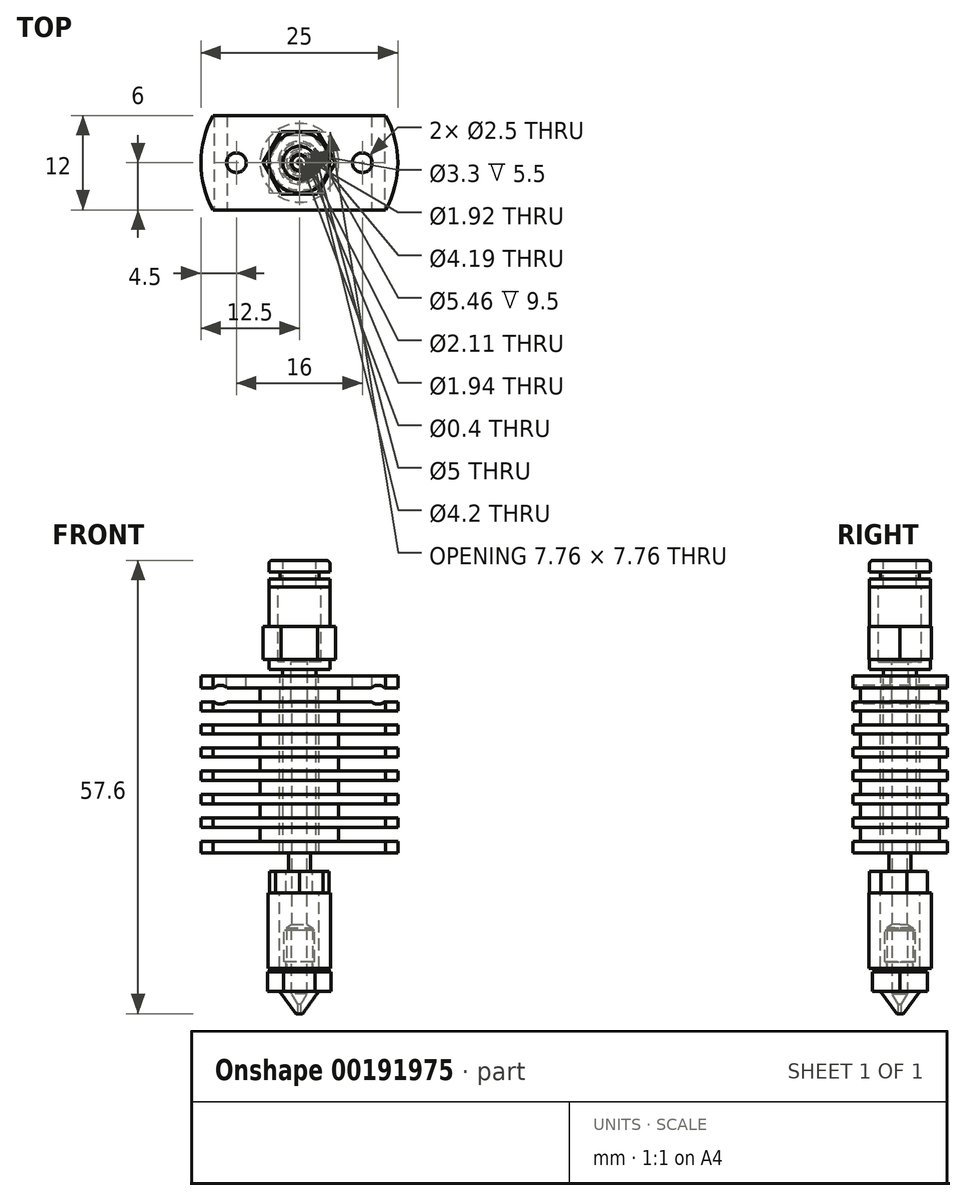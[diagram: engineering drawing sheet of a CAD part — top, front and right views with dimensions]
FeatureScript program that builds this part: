
annotation { "Feature Type Name" : "Feature", "Feature Type Description" : "" }
export const myFeature = defineFeature(function(context is Context, id is Id, definition is map)
    precondition{}
    {
        {
            var Q0;
            Q0=qCreatedBy(makeId("Front.planeOp"),FACE);
            var sketch = newSketch(context, id + "F0", { "sketchPlane" : qUnion([Q0])});
            skLineSegment(sketch, "E0.bottom", {"start": v(0, 0) * mm, "end": v(5, 0) * mm});
            skLineSegment(sketch, "E0.top", {"start": v(0, -22.5) * mm, "end": v(5, -22.5) * mm});
            skLineSegment(sketch, "E0.left", {"start": v(0, 0) * mm, "end": v(0, -22.5) * mm});
            skLineSegment(sketch, "E0.right", {"start": v(5, 0) * mm, "end": v(5, -22.5) * mm});
            skLineSegment(sketch, "E1", {"start": v(0, 43.67) * mm, "end": v(0, -73.74) * mm, "construction": true});
            skLineSegment(sketch, "E2.bottom", {"start": v(0, 0) * mm, "end": v(12.5, 0) * mm});
            skLineSegment(sketch, "E2.top", {"start": v(0, -1.5) * mm, "end": v(12.5, -1.5) * mm});
            skLineSegment(sketch, "E2.left", {"start": v(0, 0) * mm, "end": v(0, -1.5) * mm});
            skLineSegment(sketch, "E2.right", {"start": v(12.5, 0) * mm, "end": v(12.5, -1.5) * mm});
            skLineSegment(sketch, "E3.bottom", {"start": v(0, -3.27) * mm, "end": v(12.5, -3.27) * mm});
            skLineSegment(sketch, "E3.top", {"start": v(0, -4.42) * mm, "end": v(12.5, -4.42) * mm});
            skLineSegment(sketch, "E3.left", {"start": v(0, -3.27) * mm, "end": v(0, -4.42) * mm});
            skLineSegment(sketch, "E3.right", {"start": v(12.5, -3.27) * mm, "end": v(12.5, -4.42) * mm});
            skLineSegment(sketch, "E4.bottom", {"start": v(0, -6.2) * mm, "end": v(12.5, -6.2) * mm});
            skLineSegment(sketch, "E4.top", {"start": v(0, -7.34) * mm, "end": v(12.5, -7.34) * mm});
            skLineSegment(sketch, "E4.left", {"start": v(0, -6.2) * mm, "end": v(0, -7.34) * mm});
            skLineSegment(sketch, "E4.right", {"start": v(12.5, -6.2) * mm, "end": v(12.5, -7.34) * mm});
            skLineSegment(sketch, "E5.bottom", {"start": v(0, -9.11) * mm, "end": v(12.5, -9.11) * mm});
            skLineSegment(sketch, "E5.top", {"start": v(0, -10.31) * mm, "end": v(12.5, -10.31) * mm});
            skLineSegment(sketch, "E5.left", {"start": v(0, -9.11) * mm, "end": v(0, -10.31) * mm});
            skLineSegment(sketch, "E5.right", {"start": v(12.5, -9.11) * mm, "end": v(12.5, -10.31) * mm});
            skLineSegment(sketch, "E6.bottom", {"start": v(0, -12.09) * mm, "end": v(12.5, -12.09) * mm});
            skLineSegment(sketch, "E6.top", {"start": v(0, -13.29) * mm, "end": v(12.5, -13.29) * mm});
            skLineSegment(sketch, "E6.left", {"start": v(0, -12.09) * mm, "end": v(0, -13.29) * mm});
            skLineSegment(sketch, "E6.right", {"start": v(12.5, -12.09) * mm, "end": v(12.5, -13.29) * mm});
            skLineSegment(sketch, "E7.bottom", {"start": v(0, -15.06) * mm, "end": v(12.5, -15.06) * mm});
            skLineSegment(sketch, "E7.top", {"start": v(0, -16.26) * mm, "end": v(12.5, -16.26) * mm});
            skLineSegment(sketch, "E7.left", {"start": v(0, -15.06) * mm, "end": v(0, -16.26) * mm});
            skLineSegment(sketch, "E7.right", {"start": v(12.5, -15.06) * mm, "end": v(12.5, -16.26) * mm});
            skLineSegment(sketch, "E8.bottom", {"start": v(0, -18.03) * mm, "end": v(12.5, -18.03) * mm});
            skLineSegment(sketch, "E8.top", {"start": v(0, -19.23) * mm, "end": v(12.5, -19.23) * mm});
            skLineSegment(sketch, "E8.left", {"start": v(0, -18.03) * mm, "end": v(0, -19.23) * mm});
            skLineSegment(sketch, "E8.right", {"start": v(12.5, -18.03) * mm, "end": v(12.5, -19.23) * mm});
            skLineSegment(sketch, "E9.bottom", {"start": v(0, -21) * mm, "end": v(12.5, -21) * mm});
            skLineSegment(sketch, "E9.top", {"start": v(0, -22.5) * mm, "end": v(12.5, -22.5) * mm});
            skLineSegment(sketch, "E9.left", {"start": v(0, -21) * mm, "end": v(0, -22.5) * mm});
            skLineSegment(sketch, "E9.right", {"start": v(12.5, -21) * mm, "end": v(12.5, -22.5) * mm});
            skLineSegment(sketch, "E10", {"start": v(12.5, -21) * mm, "end": v(12.5, -19.23) * mm, "construction": true});
            skLineSegment(sketch, "E11", {"start": v(12.5, -18.03) * mm, "end": v(12.5, -16.26) * mm, "construction": true});
            skLineSegment(sketch, "E12", {"start": v(12.5, -15.06) * mm, "end": v(12.5, -13.29) * mm, "construction": true});
            skLineSegment(sketch, "E13", {"start": v(12.5, -12.09) * mm, "end": v(12.5, -10.31) * mm, "construction": true});
            skLineSegment(sketch, "E14", {"start": v(12.5, -9.11) * mm, "end": v(12.5, -7.34) * mm, "construction": true});
            skLineSegment(sketch, "E15", {"start": v(12.5, -6.2) * mm, "end": v(12.5, -4.42) * mm, "construction": true});
            skLineSegment(sketch, "E16", {"start": v(12.5, -3.27) * mm, "end": v(12.5, -1.5) * mm, "construction": true});
            skSolve(sketch);
        }
        {
            var Q0;
            Q0=qSketchRegion(id+"F0",true);
            var Q1;
            Q1=sQuery(id+"F0.wireOp",EDGE,"E1");
            revolve(context, id + "F1", {"entities" : qUnion([Q0]), "axis" : qUnion([Q1]), "revolveType" : RevolveType.FULL});
        }
        {
            var Q0;
            Q0=qCreatedBy(makeId("Top.planeOp"),FACE);
            var sketch = newSketch(context, id + "F2", { "sketchPlane" : qUnion([Q0])});
            skLineSegment(sketch, "E17.bottom", {"start": v(-10.97, -6) * mm, "end": v(10.97, -6) * mm});
            skLineSegment(sketch, "E17.top", {"start": v(-10.97, -12.5) * mm, "end": v(10.97, -12.5) * mm});
            skLineSegment(sketch, "E17.left", {"start": v(-10.97, -6) * mm, "end": v(-10.97, -12.5) * mm});
            skLineSegment(sketch, "E17.right", {"start": v(10.97, -6) * mm, "end": v(10.97, -12.5) * mm});
            skLineSegment(sketch, "E18.bottom", {"start": v(-10.97, 6) * mm, "end": v(10.97, 6) * mm});
            skLineSegment(sketch, "E18.top", {"start": v(-10.97, 12.5) * mm, "end": v(10.97, 12.5) * mm});
            skLineSegment(sketch, "E18.left", {"start": v(-10.97, 6) * mm, "end": v(-10.97, 12.5) * mm});
            skLineSegment(sketch, "E18.right", {"start": v(10.97, 6) * mm, "end": v(10.97, 12.5) * mm});
            skSolve(sketch);
        }
        {
            var Q0;
            Q0=qSketchRegion(id+"F2",true);
            extrude(context, id + "F3", {"entities" : qUnion([Q0]), "operationType" : NewBodyOperationType.REMOVE, "endBound" : BoundingType.THROUGH_ALL, "oppositeDirection" : true, "depth" : 25 * mm});
        }
        {
            var Q0;
            Q0=makeQuery(id+"F1.opRevolve","SWEPT_FACE",FACE,{"disambiguationData":[OSD([sQuery(id+"F0.wireOp",EDGE,"E2.bottom")])]});
            var sketch = newSketch(context, id + "F4", { "sketchPlane" : qUnion([Q0])});
            skPoint(sketch, "E19", {"position": v(0, 0) * mm});
            skPoint(sketch, "E20", {"position": v(-8, 0) * mm});
            skPoint(sketch, "E21", {"position": v(8, 0) * mm});
            skSolve(sketch);
        }
        {
            var Q0;
            Q0=sQuery(id+"F4.wireOp",VERTEX,"E19");
            var Q1;
            Q1=makeQuery(id+"F1.opRevolve","SWEPT_BODY",BODY,{"disambiguationData":[OSD([sQuery(id+"F0.wireOp",EDGE,"E0.left"),sQuery(id+"F0.wireOp",EDGE,"E0.right"),sQuery(id+"F0.wireOp",EDGE,"E2.bottom"),sQuery(id+"F0.wireOp",EDGE,"E2.top"),sQuery(id+"F0.wireOp",EDGE,"E2.left"),sQuery(id+"F0.wireOp",EDGE,"E2.right"),sQuery(id+"F0.wireOp",EDGE,"E3.bottom"),sQuery(id+"F0.wireOp",EDGE,"E3.top"),sQuery(id+"F0.wireOp",EDGE,"E3.left"),sQuery(id+"F0.wireOp",EDGE,"E3.right"),sQuery(id+"F0.wireOp",EDGE,"E4.bottom"),sQuery(id+"F0.wireOp",EDGE,"E4.top"),sQuery(id+"F0.wireOp",EDGE,"E4.left"),sQuery(id+"F0.wireOp",EDGE,"E4.right"),sQuery(id+"F0.wireOp",EDGE,"E5.bottom"),sQuery(id+"F0.wireOp",EDGE,"E5.top"),sQuery(id+"F0.wireOp",EDGE,"E5.left"),sQuery(id+"F0.wireOp",EDGE,"E5.right"),sQuery(id+"F0.wireOp",EDGE,"E6.bottom"),sQuery(id+"F0.wireOp",EDGE,"E6.top"),sQuery(id+"F0.wireOp",EDGE,"E6.left"),sQuery(id+"F0.wireOp",EDGE,"E6.right"),sQuery(id+"F0.wireOp",EDGE,"E7.bottom"),sQuery(id+"F0.wireOp",EDGE,"E7.top"),sQuery(id+"F0.wireOp",EDGE,"E7.left"),sQuery(id+"F0.wireOp",EDGE,"E7.right"),sQuery(id+"F0.wireOp",EDGE,"E8.bottom"),sQuery(id+"F0.wireOp",EDGE,"E8.top"),sQuery(id+"F0.wireOp",EDGE,"E8.left"),sQuery(id+"F0.wireOp",EDGE,"E8.right"),sQuery(id+"F0.wireOp",EDGE,"E9.bottom"),sQuery(id+"F0.wireOp",EDGE,"E9.top"),sQuery(id+"F0.wireOp",EDGE,"E9.left"),sQuery(id+"F0.wireOp",EDGE,"E9.right")])]});
            hole(context, id + "F5", {"style" : HoleStyle.SIMPLE, "endStyle" : HoleEndStyle.THROUGH, "standardTappedOrClearance" : lookupTablePath({ "standard" : "ISO", "engagement" : "75%", "pitch" : "0.8 mm", "size" : "M5", "type" : "Tapped" }), "standardBlindInLast" : lookupTablePath({ "standard" : "ISO", "engagement" : "75%", "pitch" : "0.8 mm", "size" : "M5", "type" : "Tapped" }), "holeDiameter" : 4.2 * mm, "locations" : qUnion([Q0]), "scope" : qUnion([Q1]), "isTappedThrough" : true, "majorDiameter" : 5 * mm, "showTappedDepth" : true});
        }
        {
            var Q0;
            Q0=sQuery(id+"F4.wireOp",VERTEX,"E20");
            var Q1;
            Q1=sQuery(id+"F4.wireOp",VERTEX,"E21");
            var Q2;
            Q2=makeQuery(id+"F1.opRevolve","SWEPT_BODY",BODY,{"disambiguationData":[OSD([sQuery(id+"F0.wireOp",EDGE,"E0.left"),sQuery(id+"F0.wireOp",EDGE,"E0.right"),sQuery(id+"F0.wireOp",EDGE,"E2.bottom"),sQuery(id+"F0.wireOp",EDGE,"E2.top"),sQuery(id+"F0.wireOp",EDGE,"E2.left"),sQuery(id+"F0.wireOp",EDGE,"E2.right"),sQuery(id+"F0.wireOp",EDGE,"E3.bottom"),sQuery(id+"F0.wireOp",EDGE,"E3.top"),sQuery(id+"F0.wireOp",EDGE,"E3.left"),sQuery(id+"F0.wireOp",EDGE,"E3.right"),sQuery(id+"F0.wireOp",EDGE,"E4.bottom"),sQuery(id+"F0.wireOp",EDGE,"E4.top"),sQuery(id+"F0.wireOp",EDGE,"E4.left"),sQuery(id+"F0.wireOp",EDGE,"E4.right"),sQuery(id+"F0.wireOp",EDGE,"E5.bottom"),sQuery(id+"F0.wireOp",EDGE,"E5.top"),sQuery(id+"F0.wireOp",EDGE,"E5.left"),sQuery(id+"F0.wireOp",EDGE,"E5.right"),sQuery(id+"F0.wireOp",EDGE,"E6.bottom"),sQuery(id+"F0.wireOp",EDGE,"E6.top"),sQuery(id+"F0.wireOp",EDGE,"E6.left"),sQuery(id+"F0.wireOp",EDGE,"E6.right"),sQuery(id+"F0.wireOp",EDGE,"E7.bottom"),sQuery(id+"F0.wireOp",EDGE,"E7.top"),sQuery(id+"F0.wireOp",EDGE,"E7.left"),sQuery(id+"F0.wireOp",EDGE,"E7.right"),sQuery(id+"F0.wireOp",EDGE,"E8.bottom"),sQuery(id+"F0.wireOp",EDGE,"E8.top"),sQuery(id+"F0.wireOp",EDGE,"E8.left"),sQuery(id+"F0.wireOp",EDGE,"E8.right"),sQuery(id+"F0.wireOp",EDGE,"E9.bottom"),sQuery(id+"F0.wireOp",EDGE,"E9.top"),sQuery(id+"F0.wireOp",EDGE,"E9.left"),sQuery(id+"F0.wireOp",EDGE,"E9.right")])]});
            hole(context, id + "F6", {"style" : HoleStyle.SIMPLE, "endStyle" : HoleEndStyle.BLIND, "standardTappedOrClearance" : lookupTablePath({ "standard" : "ISO", "engagement" : "75%", "pitch" : "0.5 mm", "size" : "M3", "type" : "Tapped" }), "standardBlindInLast" : lookupTablePath({ "standard" : "ISO", "engagement" : "75%", "pitch" : "0.5 mm", "size" : "M3", "type" : "Tapped" }), "holeDiameter" : 2.5 * mm, "holeDepth" : 2 * mm, "startFromSketch" : true, "locations" : qUnion([Q0, Q1]), "scope" : qUnion([Q2]), "majorDiameter" : 3 * mm});
        }
        {
            var Q0;
            Q0=qCreatedBy(makeId("Front.planeOp"),FACE);
            var sketch = newSketch(context, id + "F7", { "sketchPlane" : qUnion([Q0])});
            skLineSegment(sketch, "E22.bottom", {"start": v(0, -3.22) * mm, "end": v(1.39, -3.22) * mm});
            skLineSegment(sketch, "E22.top", {"start": v(0, -37.5) * mm, "end": v(1.39, -37.5) * mm});
            skLineSegment(sketch, "E22.left", {"start": v(0, -3.22) * mm, "end": v(0, -37.5) * mm});
            skLineSegment(sketch, "E22.right", {"start": v(1.38, -3.22) * mm, "end": v(1.39, -37.5) * mm});
            skLineSegment(sketch, "E23", {"start": v(0, 12.08) * mm, "end": v(0, -40.12) * mm, "construction": true});
            skLineSegment(sketch, "E24.bottom", {"start": v(0, -37.5) * mm, "end": v(2.5, -37.5) * mm});
            skLineSegment(sketch, "E24.top", {"start": v(0, -24.8) * mm, "end": v(2.5, -24.8) * mm});
            skLineSegment(sketch, "E24.left", {"start": v(0, -37.5) * mm, "end": v(0, -24.8) * mm});
            skLineSegment(sketch, "E24.right", {"start": v(2.5, -37.5) * mm, "end": v(2.5, -24.8) * mm});
            skLineSegment(sketch, "E25.bottom", {"start": v(0, -3.22) * mm, "end": v(2.5, -3.22) * mm});
            skLineSegment(sketch, "E25.top", {"start": v(0, -22.5) * mm, "end": v(2.5, -22.5) * mm});
            skLineSegment(sketch, "E25.left", {"start": v(0, -3.22) * mm, "end": v(0, -22.5) * mm});
            skLineSegment(sketch, "E25.right", {"start": v(2.5, -3.22) * mm, "end": v(2.5, -22.5) * mm});
            skSolve(sketch);
        }
        {
            var Q0;
            Q0=qSketchRegion(id+"F7",true);
            var Q1;
            Q1=sQuery(id+"F7.wireOp",EDGE,"E23");
            revolve(context, id + "F8", {"entities" : qUnion([Q0]), "axis" : qUnion([Q1]), "revolveType" : RevolveType.FULL});
        }
        {
            var Q0;
            Q0=makeQuery(id+"F8.opRevolve","SWEPT_FACE",FACE,{"disambiguationData":[OSD([sQuery(id+"F7.wireOp",EDGE,"E24.top")])]});
            var sketch = newSketch(context, id + "F9", { "sketchPlane" : qUnion([Q0])});
            skCircle(sketch, "E26.cCircle", {"center": v(0, 0) * mm, "radius": 3.5 * mm, "construction": true});
            skLineSegment(sketch, "E26.0", {"start": v(1.69, 3.5) * mm, "end": v(3.79, 0.86) * mm});
            skLineSegment(sketch, "E26.1", {"start": v(3.79, 0.86) * mm, "end": v(3.04, -2.42) * mm});
            skLineSegment(sketch, "E26.2", {"start": v(3.04, -2.42) * mm, "end": v(0, -3.88) * mm});
            skLineSegment(sketch, "E26.3", {"start": v(0, -3.88) * mm, "end": v(-3.04, -2.42) * mm});
            skLineSegment(sketch, "E26.4", {"start": v(-3.04, -2.42) * mm, "end": v(-3.79, 0.86) * mm});
            skLineSegment(sketch, "E26.5", {"start": v(-3.79, 0.86) * mm, "end": v(-1.69, 3.5) * mm});
            skLineSegment(sketch, "E26.6", {"start": v(-1.69, 3.5) * mm, "end": v(1.69, 3.5) * mm});
            skPoint(sketch, "E26.0.midPoint", {"position": v(2.74, 2.18) * mm});
            skSolve(sketch);
        }
        {
            var Q0;
            Q0=qSketchRegion(id+"F9",true);
            extrude(context, id + "F10", {"entities" : qUnion([Q0]), "operationType" : NewBodyOperationType.ADD, "oppositeDirection" : true, "depth" : 2.75 * mm});
        }
        {
            var Q0;
            Q0=makeQuery(id+"F8.opRevolve","SWEPT_FACE",FACE,{"disambiguationData":[OSD([sQuery(id+"F7.wireOp",EDGE,"E24.bottom")])]});
            var sketch = newSketch(context, id + "F11", { "sketchPlane" : qUnion([Q0])});
            skPoint(sketch, "E27", {"position": v(0, 0) * mm});
            skSolve(sketch);
        }
        {
            var Q0;
            Q0=sQuery(id+"F11.wireOp",VERTEX,"E27");
            var Q1;
            Q1=makeQuery(id+"F8.opRevolve","SWEPT_BODY",BODY,{"disambiguationData":[OSD([sQuery(id+"F7.wireOp",EDGE,"E22.left"),sQuery(id+"F7.wireOp",EDGE,"E22.right"),sQuery(id+"F7.wireOp",EDGE,"E24.bottom"),sQuery(id+"F7.wireOp",EDGE,"E24.top"),sQuery(id+"F7.wireOp",EDGE,"E24.left"),sQuery(id+"F7.wireOp",EDGE,"E24.right"),sQuery(id+"F7.wireOp",EDGE,"E25.bottom"),sQuery(id+"F7.wireOp",EDGE,"E25.top"),sQuery(id+"F7.wireOp",EDGE,"E25.left"),sQuery(id+"F7.wireOp",EDGE,"E25.right")])]});
            hole(context, id + "F12", {"style" : HoleStyle.SIMPLE, "endStyle" : HoleEndStyle.BLIND, "standardTappedOrClearance" : lookupTablePath({ "standard" : "ISO", "engagement" : "75%", "pitch" : "0.7 mm", "size" : "M4", "type" : "Tapped" }), "standardBlindInLast" : lookupTablePath({ "standard" : "ISO", "engagement" : "75%", "pitch" : "0.7 mm", "size" : "M4", "type" : "Tapped" }), "holeDiameter" : 3.3 * mm, "holeDepth" : 5.5 * mm, "startFromSketch" : true, "locations" : qUnion([Q0]), "scope" : qUnion([Q1]), "majorDiameter" : 4 * mm});
        }
        {
            var Q0;
            Q0=makeQuery(id+"F8.opRevolve","SWEPT_FACE",FACE,{"disambiguationData":[OSD([sQuery(id+"F7.wireOp",EDGE,"E25.bottom")])]});
            var sketch = newSketch(context, id + "F13", { "sketchPlane" : qUnion([Q0])});
            skCircle(sketch, "E28", {"center": v(0, 0) * mm, "radius": 0.96 * mm});
            skSolve(sketch);
        }
        {
            var Q0;
            Q0=qSketchRegion(id+"F13",true);
            extrude(context, id + "F14", {"entities" : qUnion([Q0]), "operationType" : NewBodyOperationType.REMOVE, "endBound" : BoundingType.THROUGH_ALL, "oppositeDirection" : true, "depth" : 25 * mm});
        }
        {
            var Q0;
            Q0=makeQuery(id+"F10.opExtrude","CAP_FACE",FACE,{"disambiguationData":[OSD([sQuery(id+"F9.wireOp",EDGE,"E26.0"),sQuery(id+"F9.wireOp",EDGE,"E26.1"),sQuery(id+"F9.wireOp",EDGE,"E26.2"),sQuery(id+"F9.wireOp",EDGE,"E26.3"),sQuery(id+"F9.wireOp",EDGE,"E26.4"),sQuery(id+"F9.wireOp",EDGE,"E26.5"),sQuery(id+"F9.wireOp",EDGE,"E26.6")])],"isStart":false});
            var sketch = newSketch(context, id + "F15", { "sketchPlane" : qUnion([Q0])});
            skCircle(sketch, "E29", {"center": v(0, 0) * mm, "radius": 2.5 * mm});
            skCircle(sketch, "E30", {"center": v(0, 0) * mm, "radius": 3.96 * mm});
            skSolve(sketch);
        }
        {
            var Q0;
            Q0=qSketchRegion(id+"F15",true);
            extrude(context, id + "F16", {"entities" : qUnion([Q0]), "depth" : 9.6 * mm});
        }
        {
            var Q0;
            Q0=qCreatedBy(makeId("Front.planeOp"),FACE);
            var sketch = newSketch(context, id + "F17", { "sketchPlane" : qUnion([Q0])});
            skLineSegment(sketch, "E31", {"start": v(0, 4.14) * mm, "end": v(0, -44.2) * mm, "construction": true});
            skLineSegment(sketch, "E32.bottom", {"start": v(0.97, -32.3) * mm, "end": v(1.95, -32.3) * mm});
            skLineSegment(sketch, "E32.top", {"start": v(0.2, -42.9) * mm, "end": v(0.41, -42.9) * mm});
            skLineSegment(sketch, "E32.right", {"start": v(3.5, -37.57) * mm, "end": v(3.5, -40.04) * mm});
            skLineSegment(sketch, "E33", {"start": v(3.5, -37.57) * mm, "end": v(1.67, -37.57) * mm});
            skLineSegment(sketch, "E34", {"start": v(1.67, -37.57) * mm, "end": v(1.67, -36.3) * mm});
            skLineSegment(sketch, "E35", {"start": v(1.67, -36.3) * mm, "end": v(1.95, -36.3) * mm});
            skLineSegment(sketch, "E36", {"start": v(1.95, -36.3) * mm, "end": v(1.95, -32.3) * mm});
            skLineSegment(sketch, "E37", {"start": v(3.5, -40.04) * mm, "end": v(2.5, -40.04) * mm});
            skLineSegment(sketch, "E38", {"start": v(2.5, -40.04) * mm, "end": v(0.41, -42.9) * mm});
            skLineSegment(sketch, "E39", {"start": v(0.2, -42.9) * mm, "end": v(0.2, -41.73) * mm});
            skLineSegment(sketch, "E40", {"start": v(0.2, -41.73) * mm, "end": v(0.97, -40.4) * mm});
            skLineSegment(sketch, "E41", {"start": v(0.97, -40.4) * mm, "end": v(0.97, -32.3) * mm});
            skPoint(sketch, "E41.endSnap0", {"position": v(0.97, -32.3) * mm});
            skPoint(sketch, "E42.orphan", {"position": v(0, -32.3) * mm});
            skSolve(sketch);
        }
        {
            var Q0;
            Q0=qSketchRegion(id+"F17",true);
            var Q1;
            Q1=sQuery(id+"F17.wireOp",EDGE,"E31");
            revolve(context, id + "F18", {"entities" : qUnion([Q0]), "axis" : qUnion([Q1]), "revolveType" : RevolveType.FULL});
        }
        {
            var Q0;
            Q0=makeQuery(id+"F18.opRevolve","SWEPT_FACE",FACE,{"disambiguationData":[OSD([sQuery(id+"F17.wireOp",EDGE,"E33")])]});
            var sketch = newSketch(context, id + "F19", { "sketchPlane" : qUnion([Q0])});
            skCircle(sketch, "E43.cCircle", {"center": v(0, 0) * mm, "radius": 3.5 * mm, "construction": true});
            skLineSegment(sketch, "E43.0", {"start": v(-2.02, -3.5) * mm, "end": v(-4.04, 0) * mm});
            skLineSegment(sketch, "E43.1", {"start": v(-4.04, 0) * mm, "end": v(-2.02, 3.5) * mm});
            skLineSegment(sketch, "E43.2", {"start": v(-2.02, 3.5) * mm, "end": v(2.02, 3.5) * mm});
            skLineSegment(sketch, "E43.3", {"start": v(2.02, 3.5) * mm, "end": v(4.04, 0) * mm});
            skLineSegment(sketch, "E43.4", {"start": v(4.04, 0) * mm, "end": v(2.02, -3.5) * mm});
            skLineSegment(sketch, "E43.5", {"start": v(2.02, -3.5) * mm, "end": v(-2.02, -3.5) * mm});
            skPoint(sketch, "E43.0.midPoint", {"position": v(-3.03, -1.75) * mm});
            skCircle(sketch, "E44.0", {"center": v(0, 0) * mm, "radius": 0.97 * mm});
            skSolve(sketch);
        }
        {
            var Q0;
            Q0=qSketchRegion(id+"F19",true);
            var Q1;
            Q1=makeQuery(id+"F18.opRevolve","SWEPT_FACE",FACE,{"disambiguationData":[OSD([sQuery(id+"F17.wireOp",EDGE,"E37")])]});
            extrude(context, id + "F20", {"entities" : qUnion([Q0]), "operationType" : NewBodyOperationType.ADD, "endBound" : BoundingType.UP_TO_SURFACE, "oppositeDirection" : true, "endBoundEntityFace" : qUnion([Q1]), "depth" : 25 * mm});
        }
        {
            var Q0;
            Q0=qCreatedBy(makeId("Front.planeOp"),FACE);
            var sketch = newSketch(context, id + "F21", { "sketchPlane" : qUnion([Q0])});
            skLineSegment(sketch, "E45", {"start": v(0, 6.79) * mm, "end": v(0, -19.22) * mm, "construction": true});
            skLineSegment(sketch, "E46.bottom", {"start": v(2.73, 11.3) * mm, "end": v(3.88, 11.3) * mm});
            skLineSegment(sketch, "E46.top", {"start": v(2.1, 0.8) * mm, "end": v(3.88, 0.8) * mm});
            skLineSegment(sketch, "E46.left", {"start": v(1.05, 1.8) * mm, "end": v(1.05, -3.2) * mm});
            skLineSegment(sketch, "E46.right", {"start": v(3.88, 11.3) * mm, "end": v(3.88, 0.8) * mm});
            skLineSegment(sketch, "E47.top", {"start": v(1.05, -3.2) * mm, "end": v(2.45, -3.2) * mm});
            skLineSegment(sketch, "E47.right", {"start": v(2.45, -0.05) * mm, "end": v(2.45, -3.2) * mm});
            skLineSegment(sketch, "E48", {"start": v(2.73, 11.3) * mm, "end": v(2.73, 1.8) * mm});
            skLineSegment(sketch, "E49", {"start": v(2.73, 1.8) * mm, "end": v(1.05, 1.8) * mm});
            skPoint(sketch, "E50.orphan", {"position": v(1.05, 11.3) * mm});
            skLineSegment(sketch, "E51", {"start": v(2.45, -0.05) * mm, "end": v(2.1, -0.05) * mm});
            skLineSegment(sketch, "E52", {"start": v(2.1, -0.05) * mm, "end": v(2.1, 0.8) * mm});
            skSolve(sketch);
        }
        {
            var Q0;
            Q0=qSketchRegion(id+"F21",true);
            var Q1;
            Q1=sQuery(id+"F21.wireOp",EDGE,"E45");
            revolve(context, id + "F22", {"entities" : qUnion([Q0]), "axis" : qUnion([Q1]), "revolveType" : RevolveType.FULL});
        }
        {
            var Q0;
            Q0=makeQuery(id+"F22.opRevolve","SWEPT_FACE",FACE,{"disambiguationData":[OSD([sQuery(id+"F21.wireOp",EDGE,"E46.top")])]});
            cPlane(context, id + "F23", {"entities" : qUnion([Q0]), "cplaneType" : CPlaneType.OFFSET, "offset" : 5.5 * mm, "oppositeDirection" : true, "width" : 150 * mm, "height" : 150 * mm});
        }
        {
            var Q0;
            Q0=qCreatedBy(id+"F23.planeOp",FACE);
            var sketch = newSketch(context, id + "F24", { "sketchPlane" : qUnion([Q0])});
            skCircle(sketch, "E53.cCircle", {"center": v(0, 0) * mm, "radius": 3.98 * mm, "construction": true});
            skLineSegment(sketch, "E53.0", {"start": v(-2.3, -3.97) * mm, "end": v(-4.59, 0) * mm});
            skLineSegment(sketch, "E53.1", {"start": v(-4.59, 0) * mm, "end": v(-2.3, 3.98) * mm});
            skLineSegment(sketch, "E53.2", {"start": v(-2.3, 3.98) * mm, "end": v(2.3, 3.98) * mm});
            skLineSegment(sketch, "E53.3", {"start": v(2.3, 3.97) * mm, "end": v(4.59, 0) * mm});
            skLineSegment(sketch, "E53.4", {"start": v(4.59, 0) * mm, "end": v(2.3, -3.98) * mm});
            skLineSegment(sketch, "E53.5", {"start": v(2.3, -3.97) * mm, "end": v(-2.3, -3.97) * mm});
            skPoint(sketch, "E53.0.midPoint", {"position": v(-3.44, -1.99) * mm});
            skCircle(sketch, "E54.0", {"center": v(0, 0) * mm, "radius": 2.73 * mm});
            skSolve(sketch);
        }
        {
            var Q0;
            Q0=qSketchRegion(id+"F24",true);
            extrude(context, id + "F25", {"entities" : qUnion([Q0]), "operationType" : NewBodyOperationType.ADD, "depth" : 4.22 * mm});
        }
        {
            var Q0;
            Q0=makeQuery(id+"F3.boolean.opBoolean","COPY",FACE,{"disambiguationData":[TD([makeQuery(id+"F1.opRevolve","SWEPT_FACE",FACE,{"disambiguationData":[OSD([sQuery(id+"F0.wireOp",EDGE,"E2.bottom")])]})])],"derivedFrom":makeQuery(id+"F3.opExtrude","SWEPT_FACE",FACE,{"disambiguationData":[OSD([sQuery(id+"F2.wireOp",EDGE,"E17.bottom")])]})});
            var sketch = newSketch(context, id + "F26", { "sketchPlane" : qUnion([Q0])});
            skPoint(sketch, "E55", {"position": v(-10, -2.39) * mm});
            skPoint(sketch, "E56", {"position": v(10, -2.39) * mm});
            skLineSegment(sketch, "E57", {"start": v(0, 10.11) * mm, "end": v(0, -7.87) * mm, "construction": true});
            skLineSegment(sketch, "E58", {"start": v(-10, -3.27) * mm, "end": v(-10, -1.5) * mm, "construction": true});
            skSolve(sketch);
        }
        {
            var Q0;
            Q0=sQuery(id+"F26.wireOp",VERTEX,"E55");
            var Q1;
            Q1=sQuery(id+"F26.wireOp",VERTEX,"E56");
            var Q2;
            Q2=makeQuery(id+"F1.opRevolve","SWEPT_BODY",BODY,{"disambiguationData":[OSD([sQuery(id+"F0.wireOp",EDGE,"E0.left"),sQuery(id+"F0.wireOp",EDGE,"E0.right"),sQuery(id+"F0.wireOp",EDGE,"E2.bottom"),sQuery(id+"F0.wireOp",EDGE,"E2.top"),sQuery(id+"F0.wireOp",EDGE,"E2.left"),sQuery(id+"F0.wireOp",EDGE,"E2.right"),sQuery(id+"F0.wireOp",EDGE,"E3.bottom"),sQuery(id+"F0.wireOp",EDGE,"E3.top"),sQuery(id+"F0.wireOp",EDGE,"E3.left"),sQuery(id+"F0.wireOp",EDGE,"E3.right"),sQuery(id+"F0.wireOp",EDGE,"E4.bottom"),sQuery(id+"F0.wireOp",EDGE,"E4.top"),sQuery(id+"F0.wireOp",EDGE,"E4.left"),sQuery(id+"F0.wireOp",EDGE,"E4.right"),sQuery(id+"F0.wireOp",EDGE,"E5.bottom"),sQuery(id+"F0.wireOp",EDGE,"E5.top"),sQuery(id+"F0.wireOp",EDGE,"E5.left"),sQuery(id+"F0.wireOp",EDGE,"E5.right"),sQuery(id+"F0.wireOp",EDGE,"E6.bottom"),sQuery(id+"F0.wireOp",EDGE,"E6.top"),sQuery(id+"F0.wireOp",EDGE,"E6.left"),sQuery(id+"F0.wireOp",EDGE,"E6.right"),sQuery(id+"F0.wireOp",EDGE,"E7.bottom"),sQuery(id+"F0.wireOp",EDGE,"E7.top"),sQuery(id+"F0.wireOp",EDGE,"E7.left"),sQuery(id+"F0.wireOp",EDGE,"E7.right"),sQuery(id+"F0.wireOp",EDGE,"E8.bottom"),sQuery(id+"F0.wireOp",EDGE,"E8.top"),sQuery(id+"F0.wireOp",EDGE,"E8.left"),sQuery(id+"F0.wireOp",EDGE,"E8.right"),sQuery(id+"F0.wireOp",EDGE,"E9.bottom"),sQuery(id+"F0.wireOp",EDGE,"E9.top"),sQuery(id+"F0.wireOp",EDGE,"E9.left"),sQuery(id+"F0.wireOp",EDGE,"E9.right")])]});
            hole(context, id + "F27", {"style" : HoleStyle.SIMPLE, "endStyle" : HoleEndStyle.THROUGH, "standardTappedOrClearance" : lookupTablePath({ "standard" : "ISO", "engagement" : "75%", "pitch" : "0.6 mm", "size" : "M3", "type" : "Tapped" }), "standardBlindInLast" : lookupTablePath({ "standard" : "ISO", "engagement" : "75%", "pitch" : "0.6 mm", "size" : "M3", "type" : "Tapped" }), "holeDiameter" : 2.4 * mm, "startFromSketch" : true, "locations" : qUnion([Q0, Q1]), "scope" : qUnion([Q2]), "isTappedThrough" : true, "showTappedDepth" : true});
        }
        {
            var Q0;
            Q0=qCreatedBy(makeId("Front.planeOp"),FACE);
            var sketch = newSketch(context, id + "F28", { "sketchPlane" : qUnion([Q0])});
            skLineSegment(sketch, "E59.top", {"start": v(3.88, 12.3) * mm, "end": v(2.47, 12.3) * mm});
            skLineSegment(sketch, "E59.left", {"start": v(3.88, 11.3) * mm, "end": v(3.88, 12.3) * mm});
            skLineSegment(sketch, "E60.bottom", {"start": v(3.88, 13.2) * mm, "end": v(2.47, 13.2) * mm});
            skLineSegment(sketch, "E60.left", {"start": v(3.88, 13.2) * mm, "end": v(3.88, 14.2) * mm});
            skLineSegment(sketch, "E61.left", {"start": v(2.47, 13.2) * mm, "end": v(2.47, 12.3) * mm});
            skLineSegment(sketch, "E61.right", {"start": v(2.1, 14.7) * mm, "end": v(2.1, 11.3) * mm});
            skLineSegment(sketch, "E62", {"start": v(3.38, 14.7) * mm, "end": v(2.1, 14.7) * mm});
            skLineSegment(sketch, "E63", {"start": v(3.88, 11.3) * mm, "end": v(2.1, 11.3) * mm});
            skLineSegment(sketch, "E64.0", {"start": v(0, 6.79) * mm, "end": v(0, -19.22) * mm, "construction": true});
            skPoint(sketch, "E65.visualSharp", {"position": v(3.88, 14.7) * mm});
            skArc(sketch, "E65.filletArc", {"start": v(3.88, 14.2) * mm, "mid": v(3.73, 14.55) * mm, "end": v(3.38, 14.7) * mm});
            skSolve(sketch);
        }
        {
            var Q0;
            Q0=qSketchRegion(id+"F28",true);
            var Q1;
            Q1=sQuery(id+"F28.wireOp",EDGE,"E64.0");
            revolve(context, id + "F29", {"entities" : qUnion([Q0]), "axis" : qUnion([Q1]), "revolveType" : RevolveType.FULL});
        }
    });
